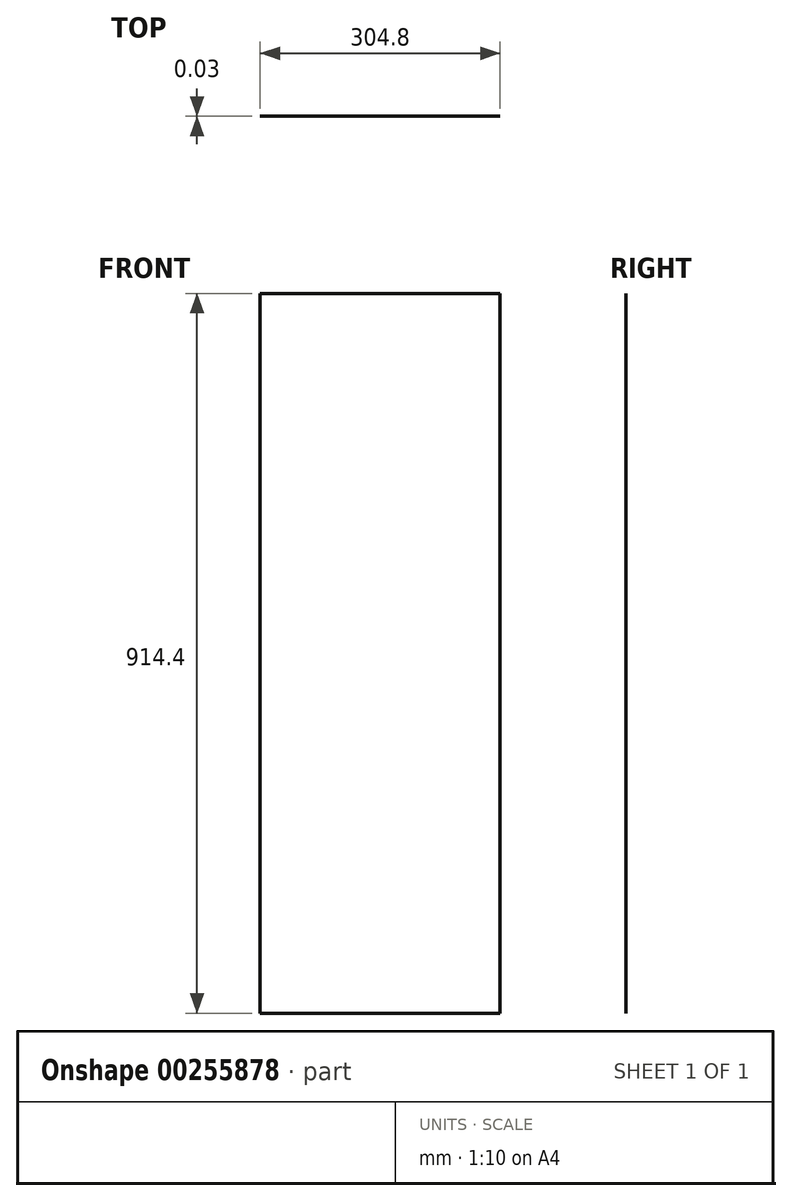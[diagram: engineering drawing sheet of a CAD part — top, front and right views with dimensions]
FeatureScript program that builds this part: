
annotation { "Feature Type Name" : "Feature", "Feature Type Description" : "" }
export const myFeature = defineFeature(function(context is Context, id is Id, definition is map)
    precondition{}
    {
        {
            var Q0;
            Q0=qCreatedBy(makeId("Front.planeOp"),FACE);
            var sketch = newSketch(context, id + "F0", { "sketchPlane" : qUnion([Q0])});
            skLineSegment(sketch, "E0.bottom", {"start": v(0, 0) * mm, "end": v(304.8, 0) * mm});
            skLineSegment(sketch, "E0.top", {"start": v(0, 914.4) * mm, "end": v(304.8, 914.4) * mm});
            skLineSegment(sketch, "E0.left", {"start": v(0, 0) * mm, "end": v(0, 914.4) * mm});
            skLineSegment(sketch, "E0.right", {"start": v(304.8, 0) * mm, "end": v(304.8, 914.4) * mm});
            skSolve(sketch);
        }
        {
            var Q0;
            Q0 = qSketchRegion(id + "F0", true);
            extrude(context, id + "F1", {"entities" : qUnion([Q0]), "depth" : 3 / 101.6 * mm});
        }
    });
